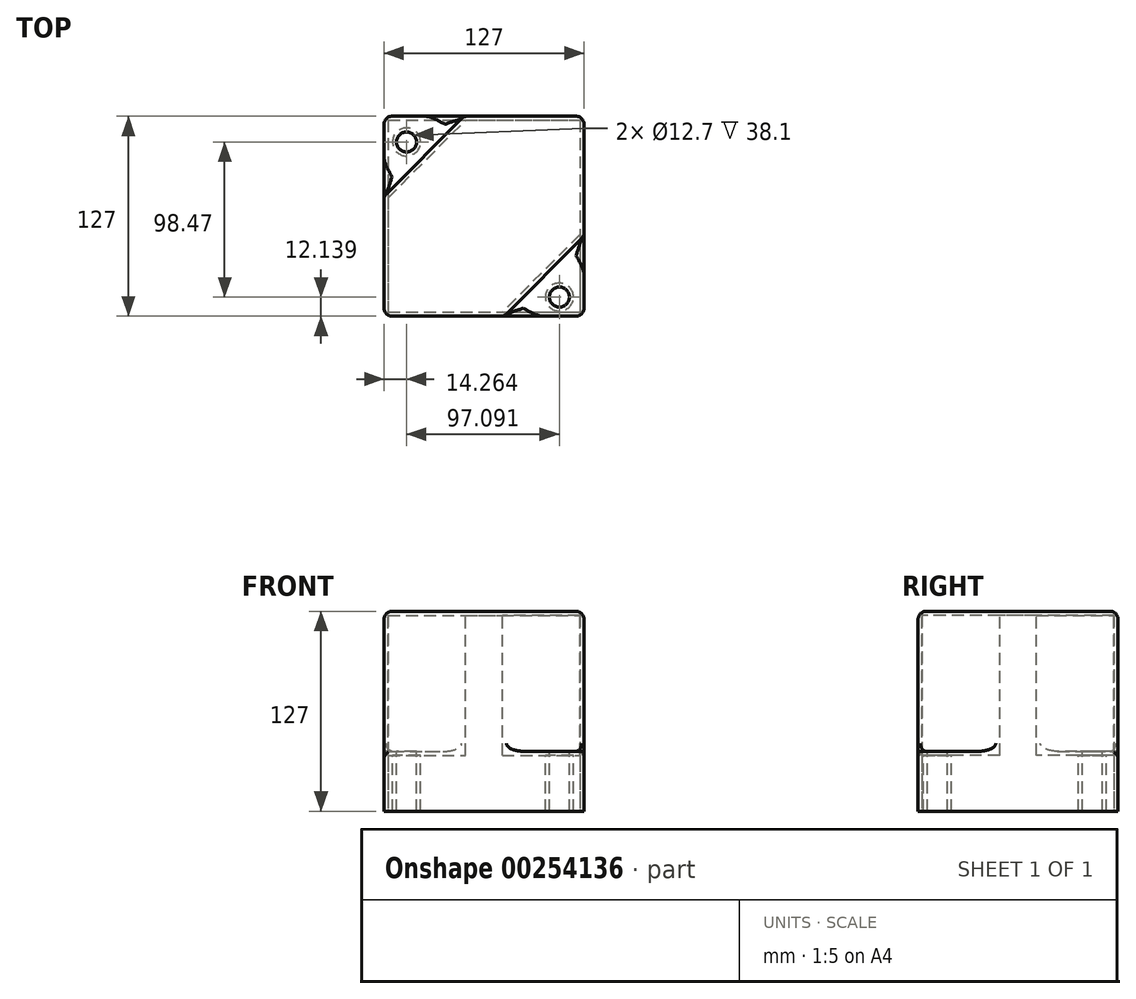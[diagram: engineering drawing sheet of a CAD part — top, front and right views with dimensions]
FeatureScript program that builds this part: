
annotation { "Feature Type Name" : "Feature", "Feature Type Description" : "" }
export const myFeature = defineFeature(function(context is Context, id is Id, definition is map)
    precondition{}
    {
        {
            var Q0;
            Q0=qCreatedBy(makeId("Top.planeOp"),FACE);
            var sketch = newSketch(context, id + "F0", { "sketchPlane" : qUnion([Q0])});
            skLineSegment(sketch, "E0.bottom", {"start": v(-54.27, 41.33) * mm, "end": v(72.73, 41.33) * mm});
            skLineSegment(sketch, "E0.top", {"start": v(-54.27, -85.67) * mm, "end": v(72.73, -85.67) * mm});
            skLineSegment(sketch, "E0.left", {"start": v(-54.27, 41.33) * mm, "end": v(-54.27, -85.67) * mm});
            skLineSegment(sketch, "E0.right", {"start": v(72.73, 41.33) * mm, "end": v(72.73, -85.67) * mm});
            skSolve(sketch);
        }
        {
            var Q0;
            Q0=makeQuery(id+"F0.imprint","IMPRINT",FACE,{"disambiguationData":[TD([[makeQuery(id+"F0.imprint","IMPRINT",EDGE,{"derivedFrom":sQuery(id+"F0.wireOp",EDGE,"E0.bottom")}),-1.0]])]});
            extrude(context, id + "F1", {"entities" : qUnion([Q0]), "depth" : 127 * mm});
        }
        {
            var Q0;
            Q0=makeQuery(id+"F1.opExtrude","CAP_FACE",FACE,{"disambiguationData":[OSD([sQuery(id+"F0.wireOp",EDGE,"E0.bottom"),sQuery(id+"F0.wireOp",EDGE,"E0.top"),sQuery(id+"F0.wireOp",EDGE,"E0.left"),sQuery(id+"F0.wireOp",EDGE,"E0.right")])],"isStart":false});
            var sketch = newSketch(context, id + "F2", { "sketchPlane" : qUnion([Q0])});
            skLineSegment(sketch, "E1", {"start": v(-54.27, 41.33) * mm, "end": v(-54.27, -9.47) * mm});
            skLineSegment(sketch, "E2", {"start": v(-54.27, -9.47) * mm, "end": v(-3.47, 41.33) * mm});
            skLineSegment(sketch, "E3", {"start": v(-3.47, 41.33) * mm, "end": v(-54.27, 41.33) * mm});
            skLineSegment(sketch, "E4", {"start": v(72.73, -85.67) * mm, "end": v(72.73, -34.87) * mm});
            skLineSegment(sketch, "E5", {"start": v(72.73, -34.87) * mm, "end": v(21.93, -85.67) * mm});
            skLineSegment(sketch, "E6", {"start": v(21.93, -85.67) * mm, "end": v(72.73, -85.67) * mm});
            skSolve(sketch);
        }
        {
            var Q0;
            Q0=makeQuery(id+"F2.imprint","IMPRINT",FACE,{"disambiguationData":[TD([[makeQuery(id+"F2.imprint","IMPRINT",EDGE,{"derivedFrom":sQuery(id+"F2.wireOp",EDGE,"E1")}),1.0]])]});
            var Q1;
            Q1=makeQuery(id+"F2.imprint","IMPRINT",FACE,{"disambiguationData":[TD([[makeQuery(id+"F2.imprint","IMPRINT",EDGE,{"derivedFrom":sQuery(id+"F2.wireOp",EDGE,"E4")}),-1.0]])]});
            extrude(context, id + "F3", {"entities" : qUnion([Q0, Q1]), "operationType" : NewBodyOperationType.REMOVE, "oppositeDirection" : true, "depth" : 88.9 * mm});
        }
        {
            var Q0;
            Q0=makeQuery(id+"F3.boolean.opBoolean","COPY",FACE,{"derivedFrom":makeQuery(id+"F3.opExtrude","CAP_FACE",FACE,{"disambiguationData":[OSD([sQuery(id+"F2.wireOp",EDGE,"E1"),sQuery(id+"F2.wireOp",EDGE,"E2"),sQuery(id+"F2.wireOp",EDGE,"E3")])],"isStart":false})});
            var sketch = newSketch(context, id + "F4", { "sketchPlane" : qUnion([Q0])});
            skCircle(sketch, "E7", {"center": v(-40, 24.94) * mm, "radius": 6.35 * mm});
            skCircle(sketch, "E8", {"center": v(57.08, -73.53) * mm, "radius": 6.35 * mm});
            skSolve(sketch);
        }
        {
            var Q0;
            Q0=makeQuery(id+"F4.imprint","IMPRINT",FACE,{"disambiguationData":[TD([[makeQuery(id+"F4.imprint","IMPRINT",EDGE,{"derivedFrom":sQuery(id+"F4.wireOp",EDGE,"E7")}),1.0]])]});
            var Q1;
            Q1=makeQuery(id+"F4.imprint","IMPRINT",FACE,{"disambiguationData":[TD([[makeQuery(id+"F4.imprint","IMPRINT",EDGE,{"derivedFrom":sQuery(id+"F4.wireOp",EDGE,"E8")}),1.0]])]});
            extrude(context, id + "F5", {"entities" : qUnion([Q0, Q1]), "operationType" : NewBodyOperationType.REMOVE, "oppositeDirection" : true, "depth" : 203.2 * mm});
        }
        {
            var Q0;
            Q0=makeQuery(id+"F1.opExtrude","CAP_FACE",FACE,{"disambiguationData":[OSD([sQuery(id+"F0.wireOp",EDGE,"E0.bottom"),sQuery(id+"F0.wireOp",EDGE,"E0.top"),sQuery(id+"F0.wireOp",EDGE,"E0.left"),sQuery(id+"F0.wireOp",EDGE,"E0.right")])],"isStart":true});
            shell(context, id + "F6", {"entities" : qUnion([Q0]), "thickness" : 2.54 * mm});
        }
        {
            var Q0;
            Q0=makeQuery(id+"F1.opExtrude","CAP_FACE",FACE,{"disambiguationData":[OSD([sQuery(id+"F0.wireOp",EDGE,"E0.bottom"),sQuery(id+"F0.wireOp",EDGE,"E0.top"),sQuery(id+"F0.wireOp",EDGE,"E0.left"),sQuery(id+"F0.wireOp",EDGE,"E0.right")])],"isStart":false});
            var Q1;
            Q1=makeQuery(id+"F3.boolean.opBoolean","COPY",FACE,{"derivedFrom":makeQuery(id+"F3.opExtrude","SWEPT_FACE",FACE,{"disambiguationData":[OSD([sQuery(id+"F2.wireOp",EDGE,"E5")])]})});
            var Q2;
            Q2=makeQuery(id+"F1.opExtrude","SWEPT_EDGE",EDGE,{"disambiguationData":[OSD([sQuery(id+"F0.wireOp",EDGE,"E0.top"),sQuery(id+"F0.wireOp",EDGE,"E0.right")])]});
            var Q3;
            Q3=makeQuery(id+"F1.opExtrude","SWEPT_EDGE",EDGE,{"disambiguationData":[OSD([sQuery(id+"F0.wireOp",EDGE,"E0.top"),sQuery(id+"F0.wireOp",EDGE,"E0.left")])]});
            var Q4;
            Q4=makeQuery(id+"F1.opExtrude","SWEPT_EDGE",EDGE,{"disambiguationData":[OSD([sQuery(id+"F0.wireOp",EDGE,"E0.bottom"),sQuery(id+"F0.wireOp",EDGE,"E0.right")])]});
            var Q5;
            Q5=makeQuery(id+"F3.boolean.opBoolean","COPY",FACE,{"derivedFrom":makeQuery(id+"F3.opExtrude","SWEPT_FACE",FACE,{"disambiguationData":[OSD([sQuery(id+"F2.wireOp",EDGE,"E2")])]})});
            var Q6;
            Q6=makeQuery(id+"F1.opExtrude","SWEPT_EDGE",EDGE,{"disambiguationData":[OSD([sQuery(id+"F0.wireOp",EDGE,"E0.bottom"),sQuery(id+"F0.wireOp",EDGE,"E0.left")])]});
            fillet(context, id + "F7", {"entities" : qUnion([Q0, Q1, Q2, Q3, Q4, Q5, Q6]), "radius" : 5.08 * mm, "tangentPropagation" : true, "allowEdgeOverflow" : false});
        }
    });
